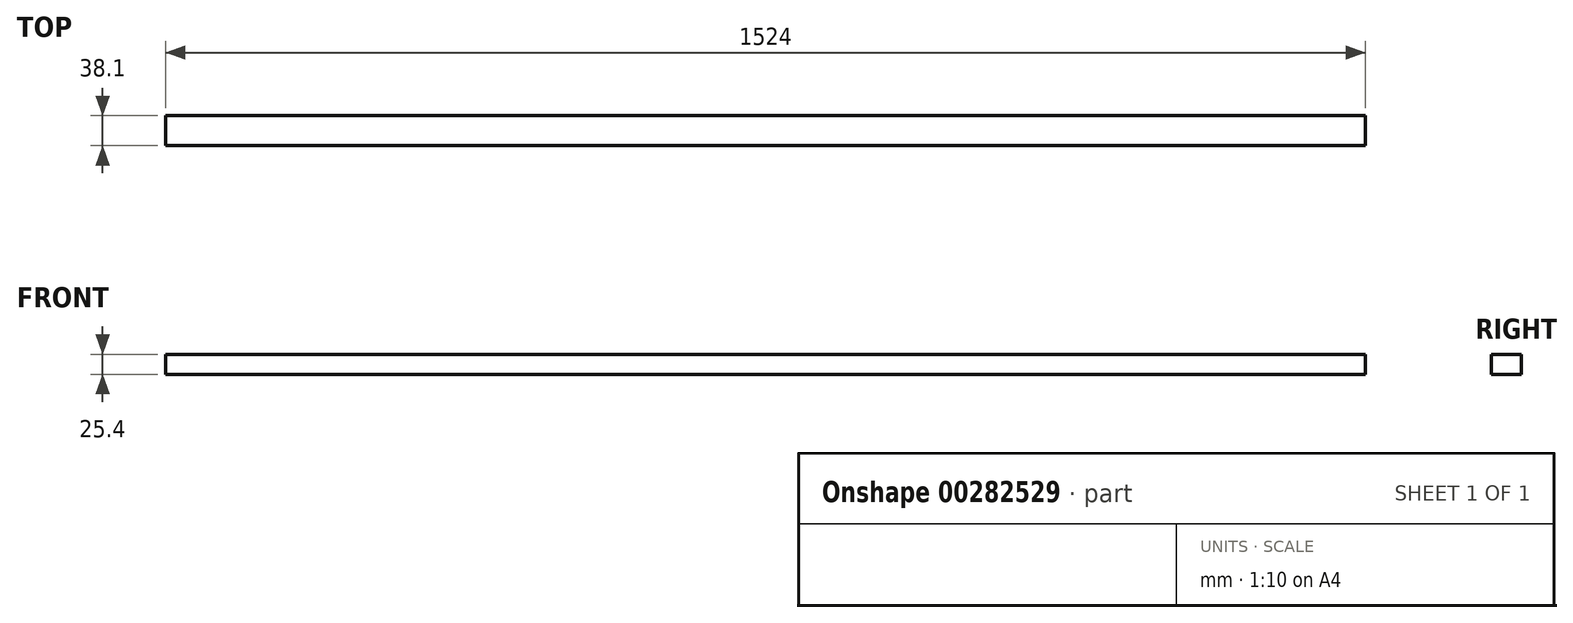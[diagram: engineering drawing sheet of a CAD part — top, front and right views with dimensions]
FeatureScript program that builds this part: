
annotation { "Feature Type Name" : "Feature", "Feature Type Description" : "" }
export const myFeature = defineFeature(function(context is Context, id is Id, definition is map)
    precondition{}
    {
        {
            var Q0;
            Q0=qCreatedBy(makeId("Front.planeOp"),FACE);
            var sketch = newSketch(context, id + "F0", { "sketchPlane" : qUnion([Q0])});
            skLineSegment(sketch, "E0.bottom", {"start": v(762, 12.7) * mm, "end": v(-762, 12.7) * mm});
            skLineSegment(sketch, "E0.top", {"start": v(762, -12.7) * mm, "end": v(-762, -12.7) * mm});
            skLineSegment(sketch, "E0.left", {"start": v(762, 12.7) * mm, "end": v(762, -12.7) * mm});
            skLineSegment(sketch, "E0.right", {"start": v(-762, 12.7) * mm, "end": v(-762, -12.7) * mm});
            skPoint(sketch, "E0.middle", {"position": v(0, 0) * mm});
            skSolve(sketch);
        }
        {
            var Q0;
            Q0=qSketchRegion(id+"F0",true);
            extrude(context, id + "F1", {"entities" : qUnion([Q0]), "endBound" : BoundingType.SYMMETRIC, "depth" : 38.1 * mm});
        }
    });
